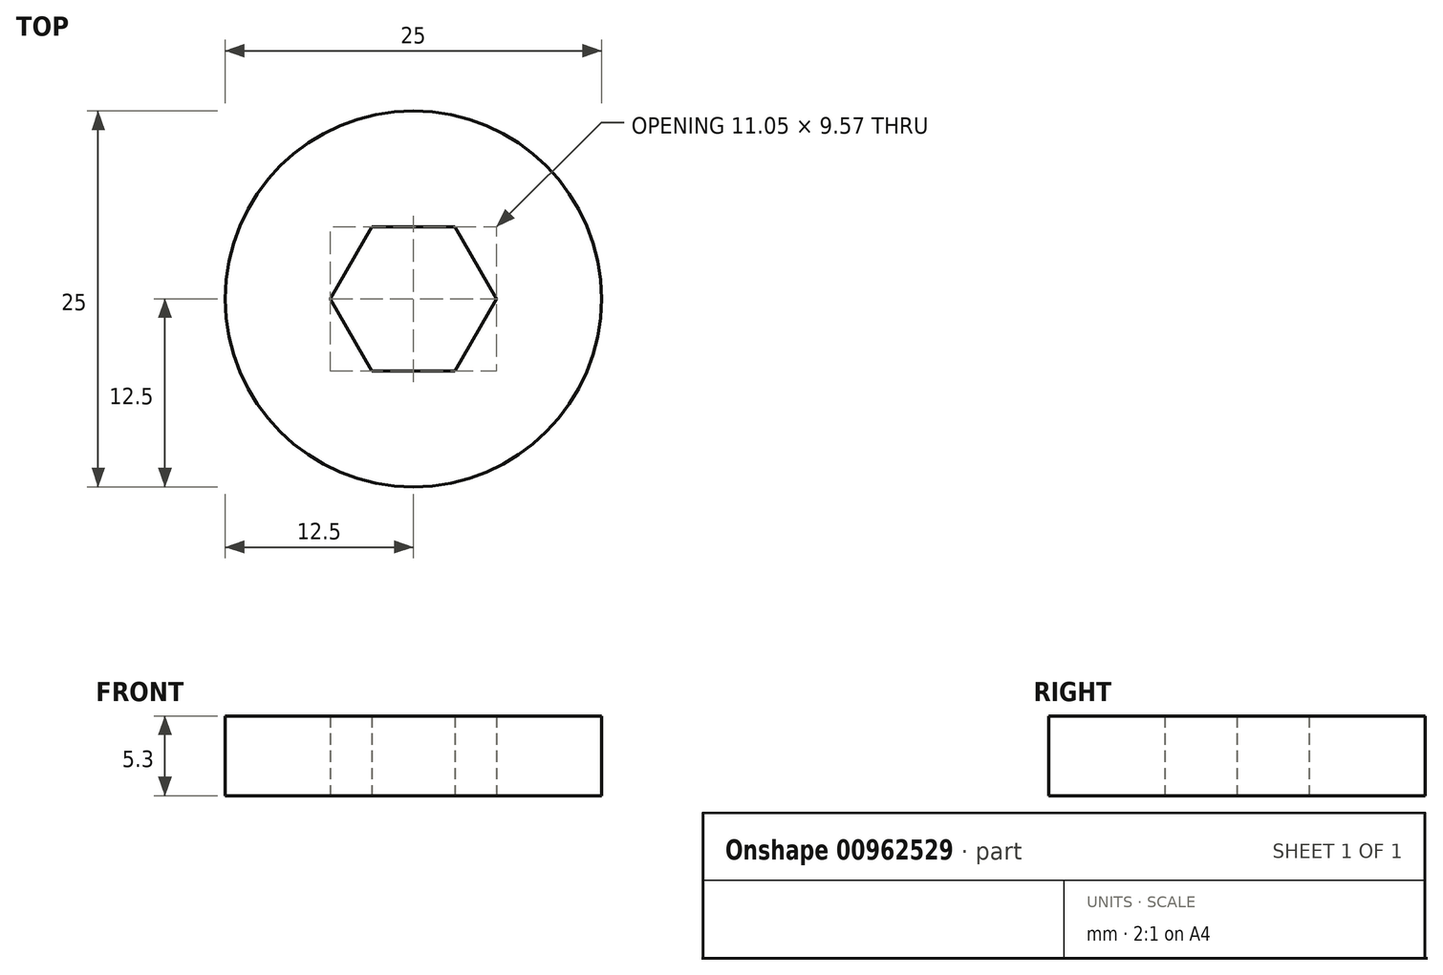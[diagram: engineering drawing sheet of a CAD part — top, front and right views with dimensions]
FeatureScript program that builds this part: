
annotation { "Feature Type Name" : "Feature", "Feature Type Description" : "" }
export const myFeature = defineFeature(function(context is Context, id is Id, definition is map)
    precondition{}
    {
        {
            var Q0;
            Q0=qCreatedBy(makeId("Top.planeOp"),FACE);
            var sketch = newSketch(context, id + "F0", { "sketchPlane" : qUnion([Q0])});
            skCircle(sketch, "E0", {"center": v(0, 0) * mm, "radius": 12.5 * mm});
            skCircle(sketch, "E1.cCircle", {"center": v(0, 0) * mm, "radius": 4.78 * mm, "construction": true});
            skLineSegment(sketch, "E1.0", {"start": v(-5.53, 0) * mm, "end": v(-2.76, 4.79) * mm});
            skLineSegment(sketch, "E1.1", {"start": v(-2.76, 4.78) * mm, "end": v(2.76, 4.78) * mm});
            skLineSegment(sketch, "E1.2", {"start": v(2.76, 4.79) * mm, "end": v(5.53, 0) * mm});
            skLineSegment(sketch, "E1.3", {"start": v(5.53, 0) * mm, "end": v(2.76, -4.78) * mm});
            skLineSegment(sketch, "E1.4", {"start": v(2.76, -4.78) * mm, "end": v(-2.76, -4.78) * mm});
            skLineSegment(sketch, "E1.5", {"start": v(-2.76, -4.78) * mm, "end": v(-5.53, 0) * mm});
            skPoint(sketch, "E1.0.midPoint", {"position": v(-4.14, 2.4) * mm});
            skSolve(sketch);
        }
        {
            var Q0;
            Q0 = qSketchRegion(id + "F0", true);
            extrude(context, id + "F1", {"entities" : qUnion([Q0]), "depth" : 5.3 * mm, "offsetDistance" : 25.4 * mm});
        }
    });
